# Revit family: EKF_EE_КомплектПоперечныхРеекВРУ-1Разборного_PROxima
name_source: partatom
category: Электрооборудование
units: mm (PartAtom-declared; Revit-internal decimal feet)

## family parameters
Всегда вертикально = Нет
На основе рабочей плоскости = Да
Общий = Да
При загрузке вырезать с полостями = Нет
Размер круглого соединителя = Использовать диаметр
Тип детали = Силовой щит
Точка расчета площади = Нет

## types (1)
- Комплект поперечных реек для ВРУ-1 R разборного (2шт.) EKF PROxima
    ADSK_Единица измерения = шт.
    ADSK_Завод-изготовитель = EKF
    ADSK_Код изделия = mb09-03-03
    ADSK_Количество = 1
    ADSK_Марка = Комплект поперечных реек
    ADSK_Масса = 0
    ADSK_Материал = Сталь_Оцинкованная
    ADSK_Наименование = Комплект поперечных реек для ВРУ-1 R разборного (2шт.) EKF PROxima
    ADSK_Обозначение = Комплект поперечных реек
    ADSK_Размер_Высота = 0 мм
    ADSK_Размер_Глубина = 0 мм
    ADSK_Размер_Ширина = 0 мм
    ВысотаРеек = 50 мм
    ГлубинаРеек = 363 мм
    Изготовитель = EKF
    Отметка по умолчанию = 0 мм
    Серия номенклатуры = Unit PROxima
    Степень защиты IP = -
    ТВ = EKF_2
    Тип = 36 мм
    Тип Реек = РейкаПоперечная : 450мм
    Тип установки = -
